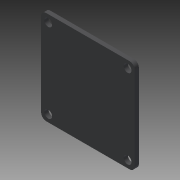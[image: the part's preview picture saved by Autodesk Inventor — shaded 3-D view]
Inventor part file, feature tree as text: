
AUTODESK INVENTOR PART (.ipt)
format: ipt  version: 2015 (Build 190159000, 159)  size: 88,064 bytes
history: native  units: mm
features: extrude x1, sketch x1
ambient origin geometry x8: Origin, YZ Plane, XZ Plane, XY Plane, X Axis, Y Axis, Z Axis, Center Point
bodies: Body1 (feature_tree)
feature tree (2):
  extrude  "Extrusion2"  Depth=1.6mm
  sketch  "Sketch3"  dims[d13=3.0mm d14=3.0mm d15=3.0mm d16=3.0mm d19=2.0mm d20=1.6mm d21=0.0mm]
